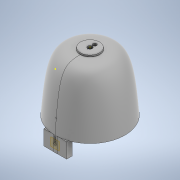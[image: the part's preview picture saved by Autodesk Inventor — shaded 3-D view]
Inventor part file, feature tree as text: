
AUTODESK INVENTOR PART (.ipt)
format: ipt  version: 2021.1 (Build 251245010, 245A)  size: 539,648 bytes
history: native  units: mm
features: sketch x11, extrude x7, plane x5, mirror x5, revolve x1, hole x1, thread x1
ambient origin geometry x8: Origin, YZ Plane, XZ Plane, XY Plane, X Axis, Y Axis, Z Axis, Center Point
bodies: Solid1 (feature_tree)
feature tree (31):
  extrude  "Extrusion1"  TaperAngle=0.0deg  [1 undecoded]
  plane  "Work Plane2"
  revolve  "Revolution1"  [1 undecoded]
  mirror  "Mirror1"
  plane  "Work Plane3"
  hole  "Hole1"  [1 undecoded]
  thread  "Thread1"  [1 undecoded]
  extrude  "Extrusion2"  Depth=178.334mm TaperAngle=0.0deg
  mirror  "Mirror2"
  extrude  "Extrusion4"  Depth=10.0mm
  sketch  "Sketch9"  dims[d36=0.0mm d40=10.0mm]
  plane  "Work Plane4"
  extrude  "Extrusion5"  Depth=25.0mm
  mirror  "Mirror4"
  extrude  "Extrusion6"  Depth=55.0mm
  sketch  "Sketch12"  dims[d46=5.0mm d49=12.0mm]
  mirror  "Mirror5"
  sketch  "Sketch13"  dims[d50=0.0mm d51=14.5mm]
  plane  "Work Plane5"
  extrude  "Extrusion7"  Depth=12.0mm
  mirror  "Mirror6"
  extrude  "Extrusion8"  Depth=14.5mm
  plane  "Work Plane1"
  sketch  "Sketch3"  dims[d1=50.0mm d3=0.0mm]
  sketch  "Sketch4"  dims[d4=25.0mm d5=-50.0mm d9=15.0mm]
  sketch  "Sketch6"  dims[d10=15.0mm d11=360.0deg d12=92.0455mm]
  sketch  "Sketch8"  dims[d16=3.0mm d17=6.0mm d18=4.0mm d19=2.0mm d20=90.0deg d21=8.0mm d22=20.594885mm d23=178.334mm d24=0.0mm]
  sketch  "Sketch10"  dims[d41=0.0mm d42=0.0mm d43=25.0mm]
  sketch  "Sketch11"  dims[d44=5.0mm d45=55.0mm]
  sketch  "Sketch14"  dims[d56=6.8mm]
  sketch  "Sketch15"  dims[d57=1.5mm d58=12.0mm d59=0.0mm d60=14.5mm d61=10.0mm d62=0.0mm d63=90.0deg d65=1.0mm d66=0.0mm d68=0.0mm d69=0.0mm]
note: 4 required parameter values undecoded (feature->parameter linkage not recoverable at this tier; creation-order binding heuristic only, values carry confidence <= 0.55)